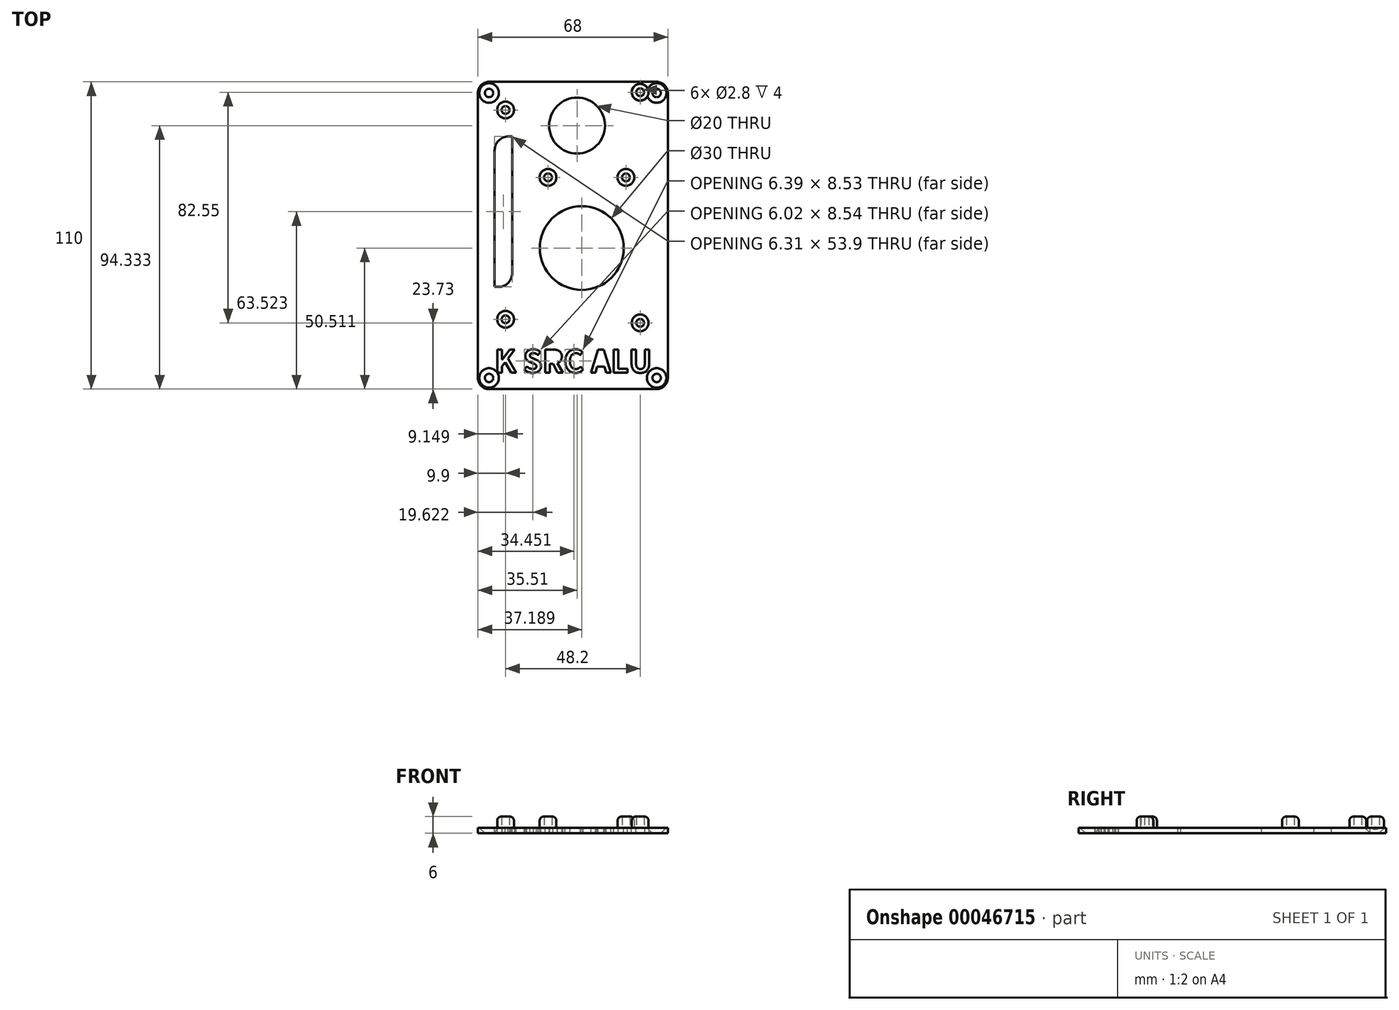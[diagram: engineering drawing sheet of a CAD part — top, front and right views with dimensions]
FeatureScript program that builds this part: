
annotation { "Feature Type Name" : "Feature", "Feature Type Description" : "" }
export const myFeature = defineFeature(function(context is Context, id is Id, definition is map)
    precondition{}
    {
        {
            var Q0;
            Q0=qCreatedBy(makeId("Top.planeOp"),FACE);
            var sketch = newSketch(context, id + "F0", { "sketchPlane" : qUnion([Q0])});
            skCircle(sketch, "E0", {"center": v(-30, 51) * mm, "radius": 1.5 * mm});
            skCircle(sketch, "E1", {"center": v(30, 51) * mm, "radius": 1.5 * mm});
            skCircle(sketch, "E2", {"center": v(30, -51) * mm, "radius": 1.5 * mm});
            skCircle(sketch, "E3", {"center": v(-30, -51) * mm, "radius": 1.5 * mm});
            skLineSegment(sketch, "E4.bottom", {"start": v(-34, 55) * mm, "end": v(34, 55) * mm});
            skLineSegment(sketch, "E4.top", {"start": v(-34, -55) * mm, "end": v(34, -55) * mm});
            skLineSegment(sketch, "E4.left", {"start": v(-34, 55) * mm, "end": v(-34, -55) * mm});
            skLineSegment(sketch, "E4.right", {"start": v(34, 55) * mm, "end": v(34, -55) * mm});
            skSolve(sketch);
        }
        {
            var Q0;
            Q0=makeQuery(id+"F0.imprint","IMPRINT",FACE,{"disambiguationData":[TD([[makeQuery(id+"F0.imprint","IMPRINT",EDGE,{"derivedFrom":sQuery(id+"F0.wireOp",EDGE,"E0")}),-1.0]])]});
            extrude(context, id + "F1", {"entities" : qUnion([Q0]), "depth" : 2 * mm});
        }
        {
            var Q0;
            Q0=makeQuery(id+"F1.opExtrude","SWEPT_EDGE",EDGE,{"disambiguationData":[OSD([sQuery(id+"F0.wireOp",EDGE,"E4.bottom"),sQuery(id+"F0.wireOp",EDGE,"E4.left")])]});
            var Q1;
            Q1=makeQuery(id+"F1.opExtrude","SWEPT_EDGE",EDGE,{"disambiguationData":[OSD([sQuery(id+"F0.wireOp",EDGE,"E4.bottom"),sQuery(id+"F0.wireOp",EDGE,"E4.right")])]});
            var Q2;
            Q2=makeQuery(id+"F1.opExtrude","SWEPT_EDGE",EDGE,{"disambiguationData":[OSD([sQuery(id+"F0.wireOp",EDGE,"E4.top"),sQuery(id+"F0.wireOp",EDGE,"E4.right")])]});
            var Q3;
            Q3=makeQuery(id+"F1.opExtrude","SWEPT_EDGE",EDGE,{"disambiguationData":[OSD([sQuery(id+"F0.wireOp",EDGE,"E4.top"),sQuery(id+"F0.wireOp",EDGE,"E4.left")])]});
            fillet(context, id + "F2", {"entities" : qUnion([Q0, Q1, Q2, Q3]), "radius" : 4 * mm, "tangentPropagation" : true, "allowEdgeOverflow" : false});
        }
        {
            var Q0;
            Q0=makeQuery(id+"F1.opExtrude","CAP_FACE",FACE,{"disambiguationData":[OSD([sQuery(id+"F0.wireOp",EDGE,"E0"),sQuery(id+"F0.wireOp",EDGE,"E1"),sQuery(id+"F0.wireOp",EDGE,"E2"),sQuery(id+"F0.wireOp",EDGE,"E3"),sQuery(id+"F0.wireOp",EDGE,"E4.bottom"),sQuery(id+"F0.wireOp",EDGE,"E4.top"),sQuery(id+"F0.wireOp",EDGE,"E4.left"),sQuery(id+"F0.wireOp",EDGE,"E4.right")])],"isStart":false});
            var sketch = newSketch(context, id + "F3", { "sketchPlane" : qUnion([Q0])});
            skCircle(sketch, "E5", {"center": v(-24.1, 44.93) * mm, "radius": 1.4 * mm});
            skCircle(sketch, "E6", {"center": v(-24.1, -30) * mm, "radius": 1.4 * mm});
            skCircle(sketch, "E7", {"center": v(24.1, -31.27) * mm, "radius": 1.4 * mm});
            skCircle(sketch, "E8", {"center": v(24.1, 51.28) * mm, "radius": 1.4 * mm});
            skCircle(sketch, "E9", {"center": v(-8.9, 20.8) * mm, "radius": 1.4 * mm});
            skCircle(sketch, "E10", {"center": v(19, 20.8) * mm, "radius": 1.4 * mm});
            skCircle(sketch, "E11", {"center": v(-24.1, 44.93) * mm, "radius": 3 * mm});
            skCircle(sketch, "E12", {"center": v(24.1, 51.28) * mm, "radius": 3 * mm});
            skCircle(sketch, "E13", {"center": v(19, 20.8) * mm, "radius": 3 * mm});
            skCircle(sketch, "E14", {"center": v(-8.9, 20.8) * mm, "radius": 3 * mm});
            skCircle(sketch, "E15", {"center": v(-24.1, -30) * mm, "radius": 3 * mm});
            skCircle(sketch, "E16", {"center": v(24.1, -31.27) * mm, "radius": 3 * mm});
            skSolve(sketch);
        }
        {
            var Q0;
            Q0=makeQuery(id+"F3.imprint","IMPRINT",FACE,{"disambiguationData":[TD([[makeQuery(id+"F3.imprint","IMPRINT",EDGE,{"derivedFrom":sQuery(id+"F3.wireOp",EDGE,"E5")}),-1.0]])]});
            var Q1;
            Q1=makeQuery(id+"F3.imprint","IMPRINT",FACE,{"disambiguationData":[TD([[makeQuery(id+"F3.imprint","IMPRINT",EDGE,{"derivedFrom":sQuery(id+"F3.wireOp",EDGE,"E8")}),-1.0]])]});
            var Q2;
            Q2=makeQuery(id+"F3.imprint","IMPRINT",FACE,{"disambiguationData":[TD([[makeQuery(id+"F3.imprint","IMPRINT",EDGE,{"derivedFrom":sQuery(id+"F3.wireOp",EDGE,"E10")}),-1.0]])]});
            var Q3;
            Q3=makeQuery(id+"F3.imprint","IMPRINT",FACE,{"disambiguationData":[TD([[makeQuery(id+"F3.imprint","IMPRINT",EDGE,{"derivedFrom":sQuery(id+"F3.wireOp",EDGE,"E9")}),-1.0]])]});
            var Q4;
            Q4=makeQuery(id+"F3.imprint","IMPRINT",FACE,{"disambiguationData":[TD([[makeQuery(id+"F3.imprint","IMPRINT",EDGE,{"derivedFrom":sQuery(id+"F3.wireOp",EDGE,"E6")}),-1.0]])]});
            var Q5;
            Q5=makeQuery(id+"F3.imprint","IMPRINT",FACE,{"disambiguationData":[TD([[makeQuery(id+"F3.imprint","IMPRINT",EDGE,{"derivedFrom":sQuery(id+"F3.wireOp",EDGE,"E7")}),-1.0]])]});
            extrude(context, id + "F4", {"entities" : qUnion([Q0, Q1, Q2, Q3, Q4, Q5]), "operationType" : NewBodyOperationType.ADD, "depth" : 4 * mm});
        }
        {
            var Q0;
            {var subQ0=sQuery(id+"F0.wireOp",EDGE,"E4.left");var subQ1=sQuery(id+"F0.wireOp",EDGE,"E4.bottom");var subQ2=sQuery(id+"F0.wireOp",EDGE,"E4.right");var subQ3=sQuery(id+"F0.wireOp",EDGE,"E4.top");var subQ4=sQuery(id+"F0.wireOp",EDGE,"E0");var subQ5=sQuery(id+"F0.wireOp",EDGE,"E1");var subQ6=sQuery(id+"F0.wireOp",EDGE,"E2");var subQ7=sQuery(id+"F0.wireOp",EDGE,"E3");Q0=makeQuery(id+"F4.boolean.opBoolean","SPLIT",FACE,{"disambiguationData":[TD([makeQuery(id+"F1.opExtrude","SWEPT_FACE",FACE,{"disambiguationData":[OSD([subQ4])]})])],"derivedFrom":makeQuery(id+"F1.opExtrude","CAP_FACE",FACE,{"disambiguationData":[OSD([subQ4,subQ5,subQ6,subQ7,subQ1,subQ3,subQ0,subQ2])],"isStart":false})});}
            var sketch = newSketch(context, id + "F5", { "sketchPlane" : qUnion([Q0])});
            skCircle(sketch, "E17", {"center": v(3.19, -4.49) * mm, "radius": 15 * mm});
            skCircle(sketch, "E18", {"center": v(1.5, 39.33) * mm, "radius": 10 * mm});
            skText(sketch, "E19", { "text": "K SRC ALU", "fontName": "NotoSansCJKsc-Bold.otf"});
            skLineSegment(sketch, "E20.bottom", {"start": v(-23, 35.47) * mm, "end": v(-21.7, 35.47) * mm});
            skLineSegment(sketch, "E20.top", {"start": v(-28, -18.43) * mm, "end": v(-26.7, -18.43) * mm});
            skLineSegment(sketch, "E20.left", {"start": v(-28, 30.47) * mm, "end": v(-28, -18.43) * mm});
            skLineSegment(sketch, "E20.right", {"start": v(-21.7, 35.47) * mm, "end": v(-21.7, -13.43) * mm});
            skPoint(sketch, "E21.visualSharp", {"position": v(-28, 35.47) * mm});
            skArc(sketch, "E21.filletArc", {"start": v(-23, 35.47) * mm, "mid": v(-26.54, 34) * mm, "end": v(-28, 30.47) * mm});
            skPoint(sketch, "E22.visualSharp", {"position": v(-21.7, -18.43) * mm});
            skArc(sketch, "E22.filletArc", {"start": v(-26.7, -18.43) * mm, "mid": v(-23.16, -16.96) * mm, "end": v(-21.7, -13.43) * mm});
            const initialGuessF5  = {"E19": [-0.028, -0.04907, 1, 0, 0.008]};
            skSetInitialGuess(sketch, initialGuessF5);
            skSolve(sketch);
        }
        {
            var Q0;
            Q0=makeQuery(id+"F5.imprint","IMPRINT",FACE,{"disambiguationData":[TD([[makeQuery(id+"F5.imprint","IMPRINT",EDGE,{"derivedFrom":sQuery(id+"F5.wireOp",EDGE,"E18")}),1.0]])]});
            var Q1;
            Q1=makeQuery(id+"F5.imprint","IMPRINT",FACE,{"disambiguationData":[TD([[makeQuery(id+"F5.imprint","IMPRINT",EDGE,{"derivedFrom":sQuery(id+"F5.wireOp",EDGE,"E17")}),1.0]])]});
            var Q2;
            Q2=makeQuery(id+"F5.imprint","IMPRINT",FACE,{"disambiguationData":[TD([[makeQuery(id+"F5.imprint","IMPRINT",EDGE,{"derivedFrom":sQuery(id+"F5.wireOp",EDGE,"E19.sketch_text.stroke-0")}),1.0]])]});
            var Q3;
            Q3=makeQuery(id+"F5.imprint","IMPRINT",FACE,{"disambiguationData":[TD([[makeQuery(id+"F5.imprint","IMPRINT",EDGE,{"derivedFrom":sQuery(id+"F5.wireOp",EDGE,"E19.sketch_text.stroke-13")}),1.0]])]});
            var Q4;
            Q4=makeQuery(id+"F5.imprint","IMPRINT",FACE,{"disambiguationData":[TD([[makeQuery(id+"F5.imprint","IMPRINT",EDGE,{"derivedFrom":sQuery(id+"F5.wireOp",EDGE,"E19.sketch_text.stroke-29")}),1.0]])]});
            var Q5;
            Q5=makeQuery(id+"F5.imprint","IMPRINT",FACE,{"disambiguationData":[TD([[makeQuery(id+"F5.imprint","IMPRINT",EDGE,{"derivedFrom":sQuery(id+"F5.wireOp",EDGE,"E19.sketch_text.stroke-29")}),-1.0]])]});
            var Q6;
            Q6=makeQuery(id+"F5.imprint","IMPRINT",FACE,{"disambiguationData":[TD([[makeQuery(id+"F5.imprint","IMPRINT",EDGE,{"derivedFrom":sQuery(id+"F5.wireOp",EDGE,"E19.sketch_text.stroke-44")}),1.0]])]});
            var Q7;
            Q7=makeQuery(id+"F5.imprint","IMPRINT",FACE,{"disambiguationData":[TD([[makeQuery(id+"F5.imprint","IMPRINT",EDGE,{"derivedFrom":sQuery(id+"F5.wireOp",EDGE,"E19.sketch_text.stroke-54")}),1.0]])]});
            var Q8;
            Q8=makeQuery(id+"F5.imprint","IMPRINT",FACE,{"disambiguationData":[TD([[makeQuery(id+"F5.imprint","IMPRINT",EDGE,{"derivedFrom":sQuery(id+"F5.wireOp",EDGE,"E19.sketch_text.stroke-54")}),-1.0]])]});
            var Q9;
            Q9=makeQuery(id+"F5.imprint","IMPRINT",FACE,{"disambiguationData":[TD([[makeQuery(id+"F5.imprint","IMPRINT",EDGE,{"derivedFrom":sQuery(id+"F5.wireOp",EDGE,"E19.sketch_text.stroke-68")}),1.0]])]});
            var Q10;
            Q10=makeQuery(id+"F5.imprint","IMPRINT",FACE,{"disambiguationData":[TD([[makeQuery(id+"F5.imprint","IMPRINT",EDGE,{"derivedFrom":sQuery(id+"F5.wireOp",EDGE,"E19.sketch_text.stroke-74")}),1.0]])]});
            var Q11;
            Q11=makeQuery(id+"F5.imprint","IMPRINT",FACE,{"disambiguationData":[TD([[makeQuery(id+"F5.imprint","IMPRINT",EDGE,{"derivedFrom":sQuery(id+"F5.wireOp",EDGE,"E20.bottom")}),-1.0]])]});
            extrude(context, id + "F6", {"entities" : qUnion([Q0, Q1, Q2, Q3, Q4, Q5, Q6, Q7, Q8, Q9, Q10, Q11]), "operationType" : NewBodyOperationType.REMOVE, "endBound" : BoundingType.THROUGH_ALL, "oppositeDirection" : true, "depth" : 25 * mm});
        }
        {
            var Q0;
            Q0=makeQuery(id+"F4.opExtrude","CAP_EDGE",EDGE,{"disambiguationData":[OSD([sQuery(id+"F3.wireOp",EDGE,"E11")])],"isStart":false});
            var Q1;
            Q1=makeQuery(id+"F4.opExtrude","CAP_EDGE",EDGE,{"disambiguationData":[OSD([sQuery(id+"F3.wireOp",EDGE,"E11")])],"isStart":true});
            var Q2;
            Q2=makeQuery(id+"F4.opExtrude","CAP_EDGE",EDGE,{"disambiguationData":[OSD([sQuery(id+"F3.wireOp",EDGE,"E14")])],"isStart":false});
            var Q3;
            Q3=makeQuery(id+"F4.opExtrude","CAP_EDGE",EDGE,{"disambiguationData":[OSD([sQuery(id+"F3.wireOp",EDGE,"E14")])],"isStart":true});
            var Q4;
            Q4=makeQuery(id+"F4.opExtrude","CAP_EDGE",EDGE,{"disambiguationData":[OSD([sQuery(id+"F3.wireOp",EDGE,"E13")])],"isStart":false});
            var Q5;
            Q5=makeQuery(id+"F4.opExtrude","CAP_EDGE",EDGE,{"disambiguationData":[OSD([sQuery(id+"F3.wireOp",EDGE,"E13")])],"isStart":true});
            var Q6;
            Q6=makeQuery(id+"F4.opExtrude","CAP_EDGE",EDGE,{"disambiguationData":[OSD([sQuery(id+"F3.wireOp",EDGE,"E15")])],"isStart":false});
            var Q7;
            Q7=makeQuery(id+"F4.opExtrude","CAP_EDGE",EDGE,{"disambiguationData":[OSD([sQuery(id+"F3.wireOp",EDGE,"E15")])],"isStart":true});
            var Q8;
            Q8=makeQuery(id+"F4.opExtrude","CAP_EDGE",EDGE,{"disambiguationData":[OSD([sQuery(id+"F3.wireOp",EDGE,"E16")])],"isStart":false});
            var Q9;
            Q9=makeQuery(id+"F4.opExtrude","CAP_EDGE",EDGE,{"disambiguationData":[OSD([sQuery(id+"F3.wireOp",EDGE,"E16")])],"isStart":true});
            var Q10;
            Q10=makeQuery(id+"F4.opExtrude","CAP_EDGE",EDGE,{"disambiguationData":[OSD([sQuery(id+"F3.wireOp",EDGE,"E12")])],"isStart":false});
            fillet(context, id + "F7", {"entities" : qUnion([Q0, Q1, Q2, Q3, Q4, Q5, Q6, Q7, Q8, Q9, Q10]), "radius" : 1.5 * mm, "tangentPropagation" : true, "allowEdgeOverflow" : false});
        }
        {
            var Q0;
            Q0=makeQuery(id+"F1.opExtrude","CAP_EDGE",EDGE,{"disambiguationData":[OSD([sQuery(id+"F0.wireOp",EDGE,"E3")])],"isStart":false});
            var Q1;
            Q1=makeQuery(id+"F1.opExtrude","CAP_EDGE",EDGE,{"disambiguationData":[OSD([sQuery(id+"F0.wireOp",EDGE,"E2")])],"isStart":false});
            var Q2;
            Q2=makeQuery(id+"F1.opExtrude","CAP_EDGE",EDGE,{"disambiguationData":[OSD([sQuery(id+"F0.wireOp",EDGE,"E1")])],"isStart":false});
            var Q3;
            Q3=makeQuery(id+"F1.opExtrude","CAP_EDGE",EDGE,{"disambiguationData":[OSD([sQuery(id+"F0.wireOp",EDGE,"E0")])],"isStart":false});
            chamfer(context, id + "F8", {"entities" : qUnion([Q0, Q1, Q2, Q3]), "width" : 2 * mm, "tangentPropagation" : true});
        }
    });
